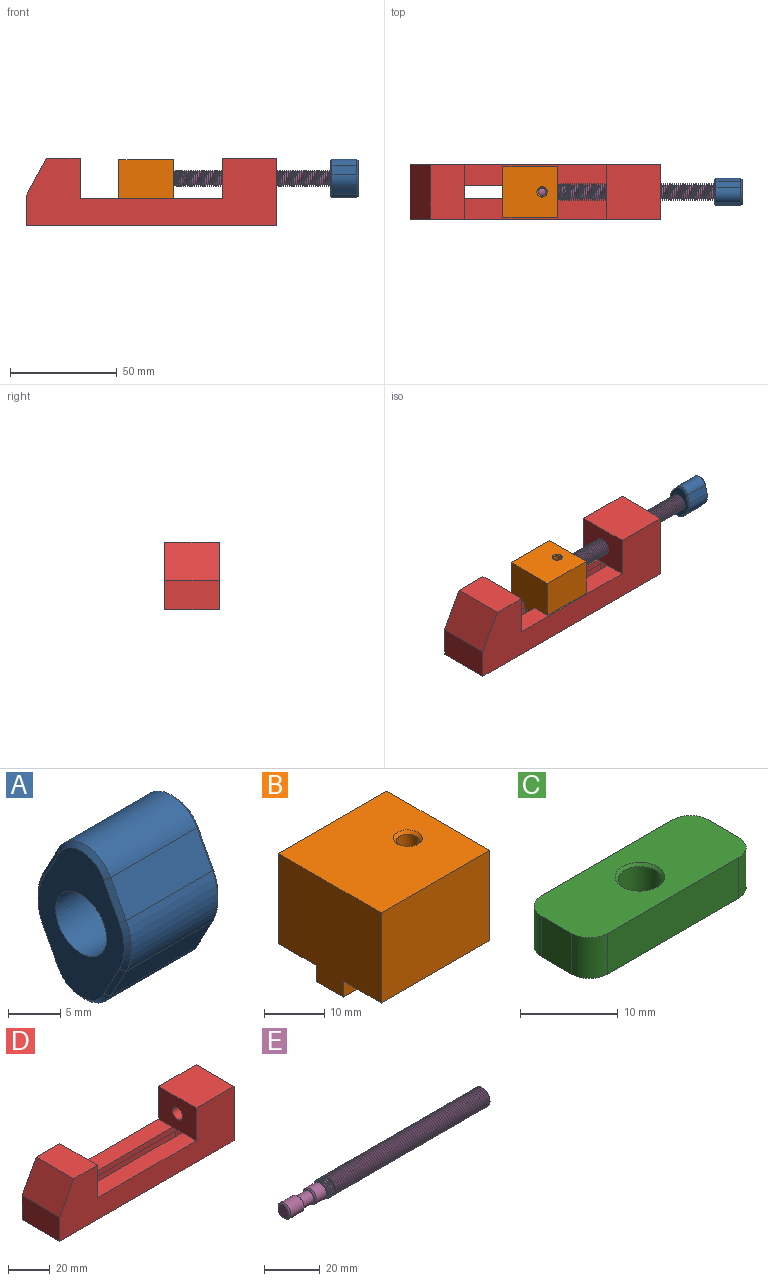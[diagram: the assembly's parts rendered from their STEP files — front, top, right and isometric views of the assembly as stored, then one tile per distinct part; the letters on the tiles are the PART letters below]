
ASSEMBLY  parts=5 mates=4
PART A: 28 faces, bbox 12.7x12.7x18.1 mm
  f0: plane 11.68x3.96mm, normal (0,0.88,0.47), area 52.4mm2, adj f1,f7,f16,f24
  f1: cylinder r=3.97mm len=11.68mm, axis (1,0,0), area 100.4mm2, adj f0,f2,f14,f22
  f2: plane 11.68x3.96mm, normal (0,-0.88,0.47), area 52.4mm2, adj f1,f3,f12,f20
  f3: cylinder r=6.35mm len=11.68mm, axis (1,0,0), area 72.4mm2, adj f2,f4,f10,f18
  f4: plane 11.68x3.96mm, normal (0,-0.88,-0.47), area 52.4mm2, adj f3,f5,f11,f19
  f5: cylinder r=3.97mm len=11.68mm, axis (1,0,0), area 100.4mm2, adj f4,f6,f13,f21
  f6: plane 11.68x3.96mm, normal (0,0.88,-0.47), area 52.4mm2, adj f5,f7,f15,f23
  f7: cylinder r=6.35mm len=11.68mm, axis (1,0,0), area 72.4mm2, adj f0,f6,f17,f25
  f8: plane 17.08x11.68mm, normal (-1,0,0), area 105.2mm2, adj f10,f11,f12,f13,f14,f15,f16,f17
  f9: plane 17.08x11.68mm, normal (1,0,0), area 142.7mm2, adj f18,f19,f20,f21,f22,f23,f24,f25
  f10: cone r=6.35mm half-angle=45deg, axis (1,0,0), area 4.3mm2, adj f3,f8,f11,f12
  f11: plane 4.2x2.55mm, normal (-0.71,-0.62,-0.33), area 3.2mm2, adj f4,f8,f10,f13
  f12: plane 4.2x2.55mm, normal (-0.71,-0.62,0.33), area 3.2mm2, adj f2,f8,f10,f14
  f13: cone r=3.97mm half-angle=45deg, axis (1,0,0), area 5.8mm2, adj f5,f8,f11,f15
  f14: cone r=3.97mm half-angle=45deg, axis (1,0,0), area 5.8mm2, adj f1,f8,f12,f16
  f15: plane 4.2x2.55mm, normal (-0.71,0.62,-0.33), area 3.2mm2, adj f6,f8,f13,f17
  f16: plane 4.2x2.55mm, normal (-0.71,0.62,0.33), area 3.2mm2, adj f0,f8,f14,f17
  f17: cone r=6.35mm half-angle=45deg, axis (1,0,0), area 4.3mm2, adj f7,f8,f15,f16
  f18: cone r=5.84mm half-angle=45deg, axis (-1,0,0), area 4.3mm2, adj f3,f9,f19,f20
  f19: plane 4.2x2.55mm, normal (0.71,-0.62,-0.33), area 3.2mm2, adj f4,f9,f18,f21
  f20: plane 4.2x2.55mm, normal (0.71,-0.62,0.33), area 3.2mm2, adj f2,f9,f18,f22
  f21: cone r=3.46mm half-angle=45deg, axis (-1,0,0), area 5.8mm2, adj f5,f9,f19,f23
  f22: cone r=3.46mm half-angle=45deg, axis (-1,0,0), area 5.8mm2, adj f1,f9,f20,f24
  f23: plane 4.2x2.55mm, normal (0.71,0.62,-0.33), area 3.2mm2, adj f6,f9,f21,f25
  f24: plane 4.2x2.55mm, normal (0.71,0.62,0.33), area 3.2mm2, adj f0,f9,f22,f25
  f25: cone r=5.84mm half-angle=45deg, axis (-1,0,0), area 4.3mm2, adj f7,f9,f23,f24
  f26: cylinder r=3.45mm len=9.53mm, axis (-1,0,0), area 206.7mm2, adj f8,f27
  f27: plane 6.91x6.91mm, normal (-1,0,0), area 37.5mm2, adj f26
PART B: 17 faces, bbox 25.4x24.1x21.5 mm
  f0: cylinder r=3.26mm len=17.27mm, axis (1,0,0), area 332.6mm2, adj f11,f12,f14,f16
  f1: plane 25.4x8.89mm, normal (0,0,-1), area 225.8mm2, adj f2,f8,f9,f10
  f2: plane 25.4x3.25mm, normal (0,-1,0), area 82.6mm2, adj f1,f3,f9,f10
  f3: plane 25.4x6.35mm, normal (0,0,-1), area 149mm2, adj f2,f4,f9,f10,f13
  f4: plane 25.4x3.25mm, normal (0,1,0), area 82.6mm2, adj f3,f5,f9,f10
  f5: plane 25.4x8.89mm, normal (0,0,-1), area 225.8mm2, adj f4,f6,f9,f10
  f6: plane 25.4x18.29mm, normal (0,1,0), area 464.5mm2, adj f5,f7,f9,f10
  f7: plane 25.4x24.13mm, normal (0,0,1), area 594.7mm2, adj f6,f8,f9,f10,f15
  f8: plane 25.4x18.29mm, normal (0,-1,0), area 464.5mm2, adj f1,f7,f9,f10
  f9: plane 24.13x21.54mm, normal (1,0,0), area 417.2mm2, adj f1,f2,f3,f4,f5,f6,f7,f8
  f10: plane 24.13x21.54mm, normal (-1,0,0), area 461.9mm2, adj f1,f2,f3,f4,f5,f6,f7,f8
  f11: plane 6.53x6.53mm, normal (1,0,0), area 33.5mm2, adj f0
  f12: cylinder r=1.73mm len=9.71mm, axis (0,0,-1), area 102.7mm2, adj f0,f13
  f13: cone r=1.73mm half-angle=41deg, axis (0,0,-1), area 4.5mm2, adj f3,f12
  f14: cylinder r=1.9mm len=5.6mm, axis (0,0,1), area 63.1mm2, adj f0,f15
  f15: cone r=1.9mm half-angle=45deg, axis (0,0,1), area 9.7mm2, adj f7,f14
  f16: cone r=3.26mm half-angle=45deg, axis (1,0,0), area 15.9mm2, adj f0,f9
PART C: 12 faces, bbox 24.1x9.5x5.1 mm
  f0: cylinder r=2.54mm len=5.08mm, axis (0,0,1), area 20.3mm2, adj f1,f7,f8,f9
  f1: plane 19.05x5.08mm, normal (0,1,0), area 96.8mm2, adj f0,f2,f8,f9
  f2: cylinder r=2.54mm len=5.08mm, axis (0,0,1), area 20.3mm2, adj f1,f3,f8,f9
  f3: plane 5.08x4.45mm, normal (-1,0,0), area 22.6mm2, adj f2,f4,f8,f9
  f4: cylinder r=2.54mm len=5.08mm, axis (0,0,1), area 20.3mm2, adj f3,f5,f8,f9
  f5: plane 19.05x5.08mm, normal (0,-1,0), area 96.8mm2, adj f4,f6,f8,f9
  f6: cylinder r=2.54mm len=5.08mm, axis (0,0,1), area 20.3mm2, adj f5,f7,f8,f9
  f7: plane 5.08x4.45mm, normal (1,0,0), area 22.6mm2, adj f0,f6,f8,f9
  f8: plane 24.13x9.53mm, normal (0,0,-1), area 208.4mm2, adj f0,f1,f2,f3,f4,f5,f6,f7
  f9: plane 24.13x9.53mm, normal (0,0,1), area 204mm2, adj f0,f1,f2,f3,f4,f5,f6,f7
  f10: cylinder r=2.25mm len=4.74mm, axis (0,0,1), area 67mm2, adj f8,f11
  f11: cone r=2.25mm half-angle=41deg, axis (0,0,1), area 6.7mm2, adj f9,f10
PART D: 28 faces, bbox 117.5x25.4x31.8 mm
  f0: plane 66.68x9.53mm, normal (0,0,1), area 635.1mm2, adj f2,f9,f10,f18
  f1: plane 66.68x9.53mm, normal (0,0,1), area 635.1mm2, adj f2,f9,f11,f20
  f2: plane 25.4x19.05mm, normal (1,0,0), area 483.9mm2, adj f0,f1,f3,f10,f11,f22
  f3: plane 25.4x15.88mm, normal (0,0,1), area 403.2mm2, adj f2,f4,f10,f11
  f4: plane 25.4x17.78mm, normal (-0.88,0,0.47), area 512.3mm2, adj f3,f5,f10,f11
  f5: plane 25.4x13.97mm, normal (-1,0,0), area 354.8mm2, adj f4,f6,f10,f11
  f6: plane 117.48x25.4mm, normal (0,0,-1), area 2118.1mm2, adj f5,f7,f10,f11,f12,f13,f14,f15
  f7: plane 31.75x25.4mm, normal (1,0,0), area 769mm2, adj f6,f8,f10,f11,f23
  f8: plane 25.4x25.4mm, normal (0,0,1), area 645.2mm2, adj f7,f9,f10,f11
  f9: plane 25.4x19.05mm, normal (-1,0,0), area 446.4mm2, adj f0,f1,f8,f10,f11,f17,f23
  f10: plane 117.48x31.75mm, normal (0,-1,0), area 2375mm2, adj f0,f2,f3,f4,f5,f6,f7,f8
  f11: plane 117.48x31.75mm, normal (0,1,0), area 2375mm2, adj f1,f2,f3,f4,f5,f6,f7,f8
  f12: plane 73.03x9.53mm, normal (0,1,0), area 695.6mm2, adj f6,f13,f15,f16
  f13: cylinder r=4.76mm len=9.53mm, axis (0,0,-1), area 142.5mm2, adj f6,f12,f14,f16
  f14: plane 73.03x9.53mm, normal (0,-1,0), area 695.6mm2, adj f6,f13,f15,f16
  f15: cylinder r=4.76mm len=9.53mm, axis (0,0,-1), area 142.5mm2, adj f6,f12,f14,f16
  f16: plane 82.55x9.53mm, normal (0,0,-1), area 271.4mm2, adj f12,f13,f14,f15,f18,f19,f20,f21
  f17: plane 6.35x6.35mm, normal (0,0,-1), area 36mm2, adj f9,f18,f20,f21
  f18: plane 73.03x3.18mm, normal (0,1,0), area 231.9mm2, adj f0,f16,f17,f19,f21,f22
  f19: cylinder r=3.17mm len=6.35mm, axis (0,0,-1), area 31.7mm2, adj f16,f18,f20,f22
  f20: plane 73.03x3.18mm, normal (0,-1,0), area 231.9mm2, adj f1,f16,f17,f19,f21,f22
  f21: cylinder r=3.17mm len=6.35mm, axis (0,0,-1), area 31.7mm2, adj f16,f17,f18,f20
  f22: plane 6.35x6.35mm, normal (0,0,-1), area 36mm2, adj f2,f18,f19,f20
  f23: cylinder r=3.45mm len=25.4mm, axis (1,0,0), area 551.3mm2, adj f7,f9
  f24: cylinder r=3.97mm len=15.88mm, axis (0,0,-1), area 395.9mm2, adj f6,f25
  f25: cone r=0mm half-angle=59deg, axis (0,0,-1), area 57.7mm2, adj f24
  f26: cylinder r=3.97mm len=15.88mm, axis (0,0,-1), area 395.9mm2, adj f6,f27
  f27: cone r=0mm half-angle=59deg, axis (0,0,-1), area 57.7mm2, adj f26
PART E: 17 faces, bbox 101.1x9.1x9.2 mm
  f0: cylinder r=3.97mm len=7.94mm, axis (-1,0,0), area 12.7mm2, adj f1,f4,f5
  f1: plane 7.94x7.94mm, normal (1,0,0), area 49.5mm2, adj f0
  f2: bspline ~82.63x9.06mm, area 1783.6mm2, adj f3,f4,f6,f9
  f3: bspline ~82.54x7.85mm, area 1792.8mm2, adj f2,f4,f5,f6,f9
  f4: plane 1.04x0.92mm, normal (0,0,1), area 0.5mm2, adj f0,f2,f3,f5
  f5: bspline ~9.17x7.94mm, area 1.3mm2, adj f0,f3,f4
  f6: cone r=3.97mm half-angle=45deg, axis (1,0,0), area 12.2mm2, adj f2,f3,f9
  f7: cylinder r=3.3mm len=6.6mm, axis (1,0,0), area 105.4mm2, adj f9,f14
  f8: plane 5.59x5.59mm, normal (-1,0,0), area 4.3mm2, adj f10,f14
  f9: plane 6.61x6.61mm, normal (1,0,0), area 4.5mm2, adj f2,f3,f6,f7
  f10: cylinder r=2.54mm len=5.33mm, axis (1,0,0), area 85.1mm2, adj f8,f12
  f11: cylinder r=3.3mm len=6.6mm, axis (-1,0,0), area 137mm2, adj f15,f16
  f12: plane 5.59x5.59mm, normal (1,0,0), area 4.3mm2, adj f10,f15
  f13: plane 5.59x5.59mm, normal (-1,0,0), area 24.5mm2, adj f16
  f14: cone r=3.3mm half-angle=45deg, axis (1,0,0), area 13.8mm2, adj f7,f8
  f15: cone r=2.79mm half-angle=45deg, axis (-1,0,0), area 13.8mm2, adj f11,f12
  f16: cone r=3.3mm half-angle=45deg, axis (1,0,0), area 13.8mm2, adj f11,f13
PLACE A rot(axis=(-1,0,0),167.4deg) t=(23.51,-30.21,20.21)mm
PLACE B t=(-88.38,-30.21,10.69)mm
PLACE C rot(axis=(1,0,0),0deg) t=(-75.68,-30.21,7.44)mm
PLACE D t=(-73.15,-30.21,-2.01)mm fixed
PLACE E rot(axis=(-1,0,0),167.4deg) t=(-62.21,-30.21,20.21)mm
MATE revolute E.f0 <-> B.f0  axis (-1,0,0) through (-80.76,-30.21,20.21)mm
MATE fastened A.f3 <-> E.f0  axis (-1,0,0) through (20.34,-30.21,20.21)mm
MATE slider B.f10 <-> D.f2  axis (-1,0,0) through (-88.38,-33.39,10.69)mm
MATE fastened C.f10 <-> B.f12  axis (0,0,1) through (-75.68,-30.21,7.44)mm
